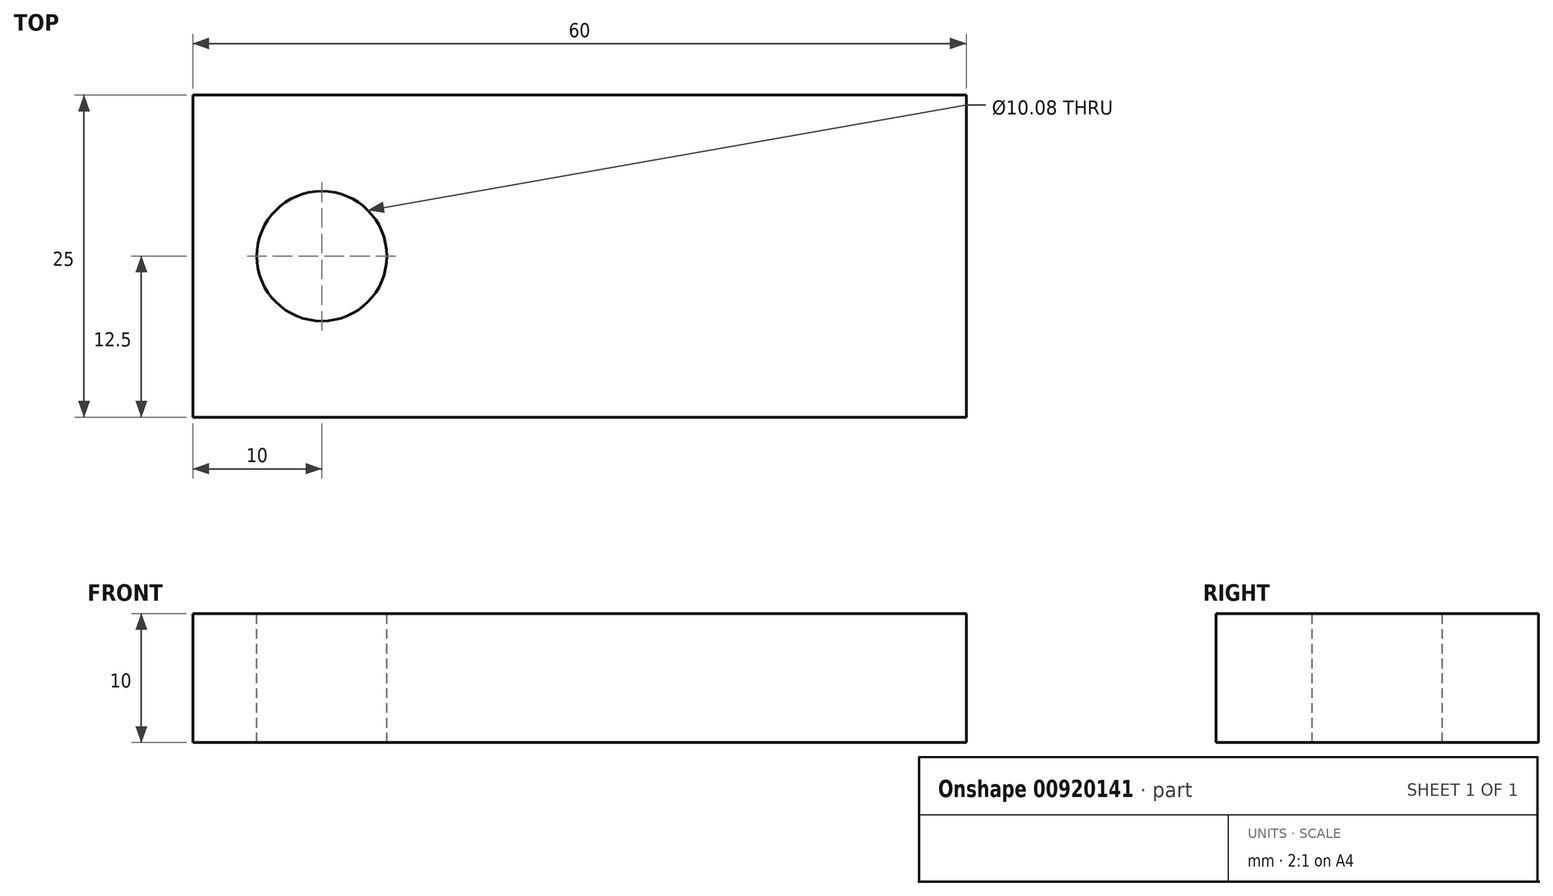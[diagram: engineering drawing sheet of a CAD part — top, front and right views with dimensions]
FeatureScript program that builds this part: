
annotation { "Feature Type Name" : "Feature", "Feature Type Description" : "" }
export const myFeature = defineFeature(function(context is Context, id is Id, definition is map)
    precondition{}
    {
        {
            var Q0;
            Q0=qCreatedBy(makeId("Front.planeOp"),FACE);
            var sketch = newSketch(context, id + "F0", { "sketchPlane" : qUnion([Q0])});
            skLineSegment(sketch, "E0.bottom", {"start": v(-30, 0) * mm, "end": v(30, 0) * mm});
            skLineSegment(sketch, "E0.top", {"start": v(-30, 10) * mm, "end": v(30, 10) * mm});
            skLineSegment(sketch, "E0.left", {"start": v(-30, 10) * mm, "end": v(-30, 0) * mm});
            skLineSegment(sketch, "E0.right", {"start": v(30, 10) * mm, "end": v(30, 0) * mm});
            skSolve(sketch);
        }
        {
            var Q0;
            Q0=qSketchRegion(id+"F0",true);
            extrude(context, id + "F1", {"entities" : qUnion([Q0]), "endBound" : BoundingType.SYMMETRIC, "depth" : 25 * mm, "offsetDistance" : 25 * mm});
        }
        {
            var Q0;
            Q0=qCreatedBy(makeId("Front.planeOp"),FACE);
            var sketch = newSketch(context, id + "F2", { "sketchPlane" : qUnion([Q0])});
            skLineSegment(sketch, "E1.bottom", {"start": v(-21, 0) * mm, "end": v(-19, 0) * mm, "construction": true});
            skLineSegment(sketch, "E1.top", {"start": v(-21, -12) * mm, "end": v(-19, -12) * mm, "construction": true});
            skLineSegment(sketch, "E1.left", {"start": v(-21, 0) * mm, "end": v(-21, -12) * mm, "construction": true});
            skLineSegment(sketch, "E1.right", {"start": v(-19, 0) * mm, "end": v(-19, -12) * mm, "construction": true});
            skLineSegment(sketch, "E2.bottom", {"start": v(-20, 0) * mm, "end": v(-20, 0) * mm});
            skLineSegment(sketch, "E2.top", {"start": v(-20, -12) * mm, "end": v(-20, -12) * mm});
            skLineSegment(sketch, "E2.left", {"start": v(-20, 0) * mm, "end": v(-20, -12) * mm, "construction": true});
            skLineSegment(sketch, "E2.right", {"start": v(-20, 0) * mm, "end": v(-20, -12) * mm, "construction": true});
            skLineSegment(sketch, "E3", {"start": v(-18.79, -13.28) * mm, "end": v(-22.08, 6.5) * mm, "construction": true});
            skLineSegment(sketch, "E4", {"start": v(-22.08, 6.5) * mm, "end": v(-25.04, 6) * mm, "construction": true});
            skLineSegment(sketch, "E5", {"start": v(-25.04, 6) * mm, "end": v(-22.04, -12) * mm, "construction": true});
            skLineSegment(sketch, "E6", {"start": v(-22.04, -12) * mm, "end": v(-18.79, -13.28) * mm, "construction": true});
            skLineSegment(sketch, "E7.bottom", {"start": v(-20, 0) * mm, "end": v(-25.04, 0) * mm});
            skLineSegment(sketch, "E7.top", {"start": v(-20, 12) * mm, "end": v(-25.04, 12) * mm});
            skLineSegment(sketch, "E7.left", {"start": v(-20, 0) * mm, "end": v(-20, 12) * mm});
            skLineSegment(sketch, "E7.right", {"start": v(-25.04, 0) * mm, "end": v(-25.04, 12) * mm});
            skSolve(sketch);
        }
        {
            var Q0;
            Q0=makeQuery(id+"F2.imprint","IMPRINT",FACE,{"disambiguationData":[TD([[makeQuery(id+"F2.imprint","IMPRINT",EDGE,{"derivedFrom":sQuery(id+"F2.wireOp",EDGE,"E7.bottom")}),-1.0]])]});
            var Q1;
            Q1=sQuery(id+"F2.wireOp",EDGE,"E7.left");
            revolve(context, id + "F3", {"operationType" : NewBodyOperationType.REMOVE, "surfaceOperationType" : NewSurfaceOperationType.NEW, "entities" : qUnion([Q0]), "axis" : qUnion([Q1]), "revolveType" : RevolveType.FULL, "oppositeDirection" : true});
        }
    });
